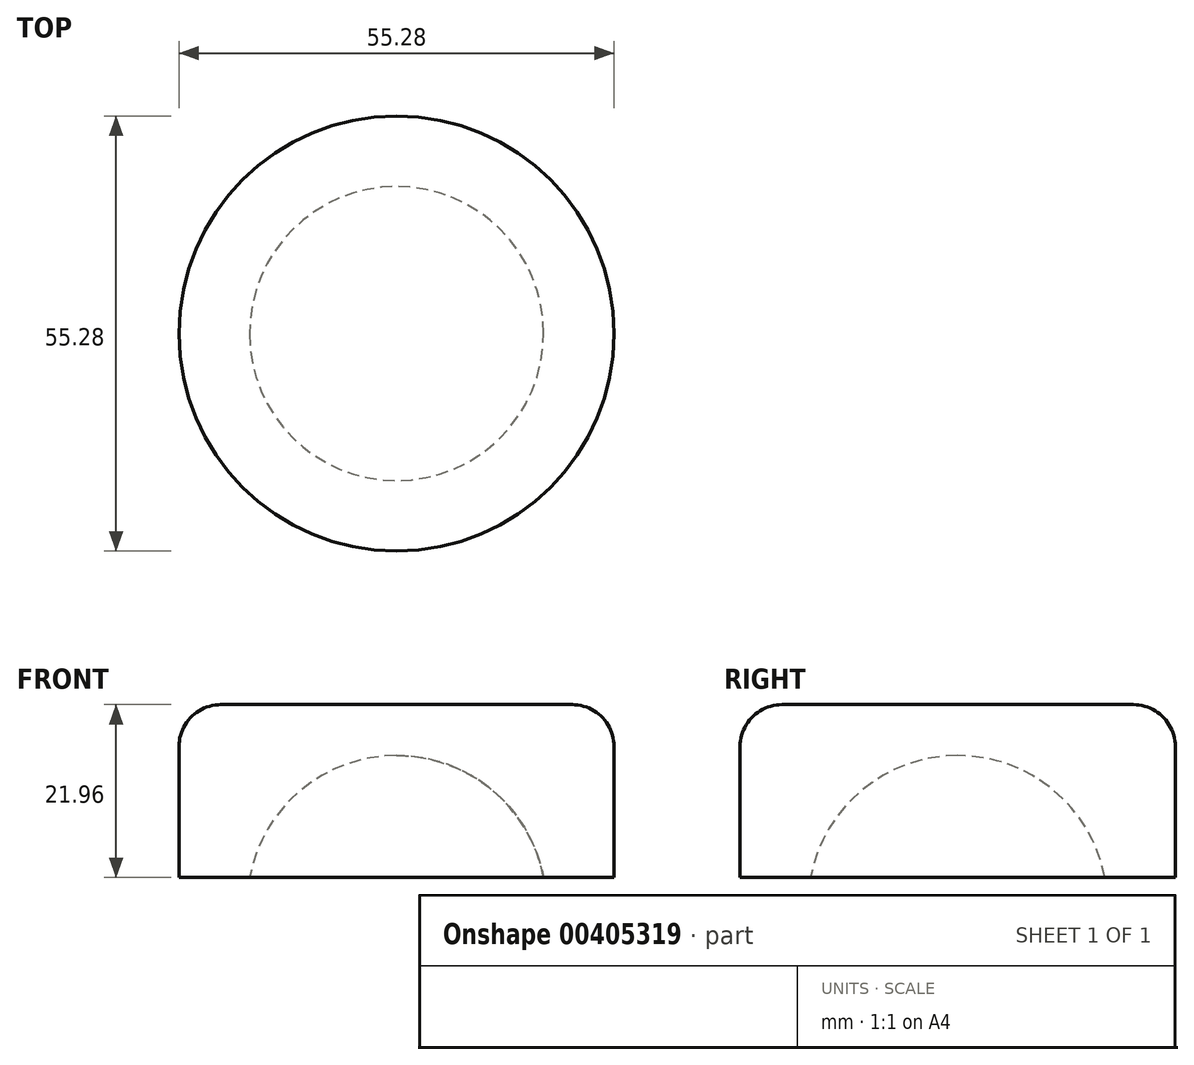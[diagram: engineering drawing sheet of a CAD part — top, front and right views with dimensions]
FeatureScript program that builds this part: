
annotation { "Feature Type Name" : "Feature", "Feature Type Description" : "" }
export const myFeature = defineFeature(function(context is Context, id is Id, definition is map)
    precondition{}
    {
        {
            var Q0;
            Q0=qCreatedBy(makeId("Front.planeOp"),FACE);
            var sketch = newSketch(context, id + "F0", { "sketchPlane" : qUnion([Q0])});
            skArc(sketch, "E0", {"start": v(0, 19) * mm, "mid": v(-12.13, 14.62) * mm, "end": v(-18.67, 3.5) * mm});
            skLineSegment(sketch, "E1.top", {"start": v(0, 25.46) * mm, "end": v(-27.64, 25.46) * mm});
            skLineSegment(sketch, "E1.right", {"start": v(-27.64, 3.5) * mm, "end": v(-27.64, 25.46) * mm});
            skLineSegment(sketch, "E2.trimOffspring", {"start": v(-18.67, 3.5) * mm, "end": v(-27.64, 3.5) * mm});
            skPoint(sketch, "E3.endSnap0", {"position": v(0, 19) * mm});
            skLineSegment(sketch, "E4", {"start": v(0, 19) * mm, "end": v(0, 25.46) * mm});
            skSolve(sketch);
        }
        {
            var Q0;
            Q0=qCreatedBy(makeId("Front.planeOp"),FACE);
            var sketch = newSketch(context, id + "F1", { "sketchPlane" : qUnion([Q0])});
            skLineSegment(sketch, "E5", {"start": v(0, 0) * mm, "end": v(0, 36.44) * mm});
            skSolve(sketch);
        }
        {
            var Q0;
            Q0=makeQuery(id+"F0.imprint","IMPRINT",FACE,{"disambiguationData":[TD([[makeQuery(id+"F0.imprint","IMPRINT",EDGE,{"derivedFrom":sQuery(id+"F0.wireOp",EDGE,"E0")}),-1.0]])]});
            var Q1;
            Q1=sQuery(id+"F1.wireOp",EDGE,"E5");
            revolve(context, id + "F2", {"entities" : qUnion([Q0]), "axis" : qUnion([Q1]), "revolveType" : RevolveType.FULL});
        }
        {
            var Q0;
            Q0=makeQuery(id+"F2.opRevolve","SWEPT_FACE",FACE,{"disambiguationData":[OSD([sQuery(id+"F0.wireOp",EDGE,"E1.top")])]});
            fillet(context, id + "F3", {"entities" : qUnion([Q0]), "radius" : 5.3 * mm, "tangentPropagation" : true, "allowEdgeOverflow" : false});
        }
    });
